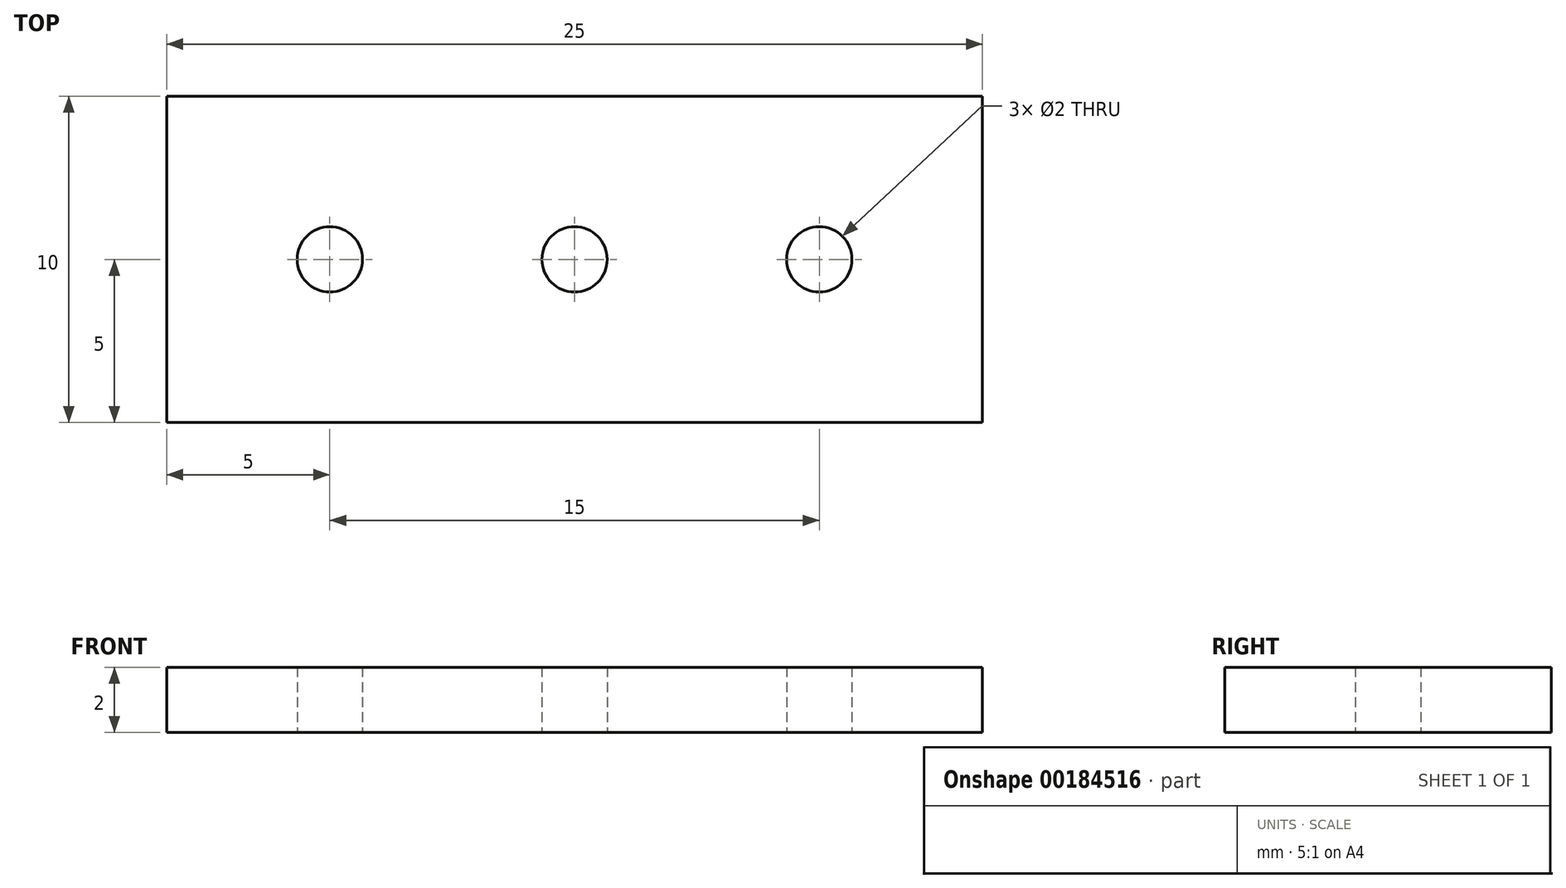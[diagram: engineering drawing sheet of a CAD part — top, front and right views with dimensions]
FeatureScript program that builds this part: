
annotation { "Feature Type Name" : "Feature", "Feature Type Description" : "" }
export const myFeature = defineFeature(function(context is Context, id is Id, definition is map)
    precondition{}
    {
        {
            var Q0;
            Q0=qCreatedBy(makeId("Top.planeOp"),FACE);
            var sketch = newSketch(context, id + "F0", { "sketchPlane" : qUnion([Q0])});
            skLineSegment(sketch, "E0.bottom", {"start": v(0, 0) * mm, "end": v(25, 0) * mm});
            skLineSegment(sketch, "E0.top", {"start": v(0, -10) * mm, "end": v(25, -10) * mm});
            skLineSegment(sketch, "E0.left", {"start": v(0, 0) * mm, "end": v(0, -10) * mm});
            skLineSegment(sketch, "E0.right", {"start": v(25, 0) * mm, "end": v(25, -10) * mm});
            skCircle(sketch, "E1", {"center": v(12.5, -5) * mm, "radius": 1 * mm});
            skCircle(sketch, "E2", {"center": v(5, -5) * mm, "radius": 1 * mm});
            skCircle(sketch, "E3", {"center": v(20, -5) * mm, "radius": 1 * mm});
            skSolve(sketch);
        }
        {
            var Q0;
            Q0=makeQuery(id+"F0.imprint","IMPRINT",FACE,{"disambiguationData":[TD([[makeQuery(id+"F0.imprint","IMPRINT",EDGE,{"derivedFrom":sQuery(id+"F0.wireOp",EDGE,"E0.bottom")}),-1.0]])]});
            extrude(context, id + "F1", {"entities" : qUnion([Q0]), "depth" : 2 * mm});
        }
    });
